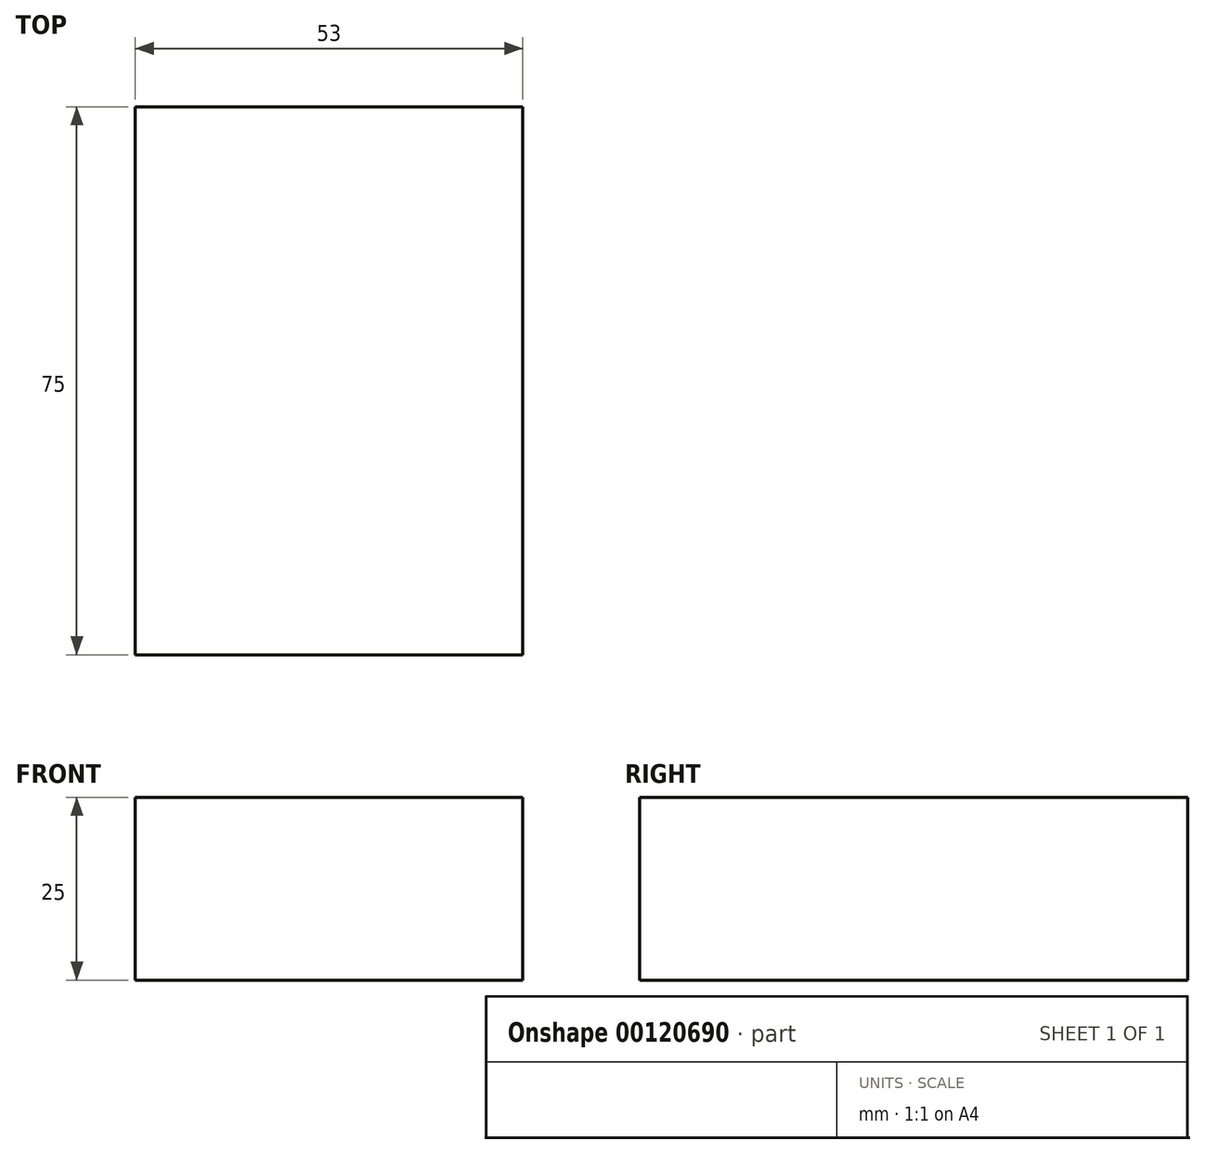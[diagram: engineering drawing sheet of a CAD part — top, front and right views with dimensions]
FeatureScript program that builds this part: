
annotation { "Feature Type Name" : "Feature", "Feature Type Description" : "" }
export const myFeature = defineFeature(function(context is Context, id is Id, definition is map)
    precondition{}
    {
        {
            var Q0;
            Q0=qCreatedBy(makeId("Top.planeOp"),FACE);
            var sketch = newSketch(context, id + "F0", { "sketchPlane" : qUnion([Q0])});
            skLineSegment(sketch, "E0.bottom", {"start": v(-55.8, 41.9) * mm, "end": v(-2.8, 41.9) * mm});
            skLineSegment(sketch, "E0.top", {"start": v(-55.8, -33.1) * mm, "end": v(-2.8, -33.1) * mm});
            skLineSegment(sketch, "E0.left", {"start": v(-55.8, 41.9) * mm, "end": v(-55.8, -33.1) * mm});
            skLineSegment(sketch, "E0.right", {"start": v(-2.8, 41.9) * mm, "end": v(-2.8, -33.1) * mm});
            skSolve(sketch);
        }
        {
            var Q0;
            Q0 = qSketchRegion(id + "F0", true);
            extrude(context, id + "F1", {"entities" : qUnion([Q0]), "depth" : 25 * mm});
        }
    });
